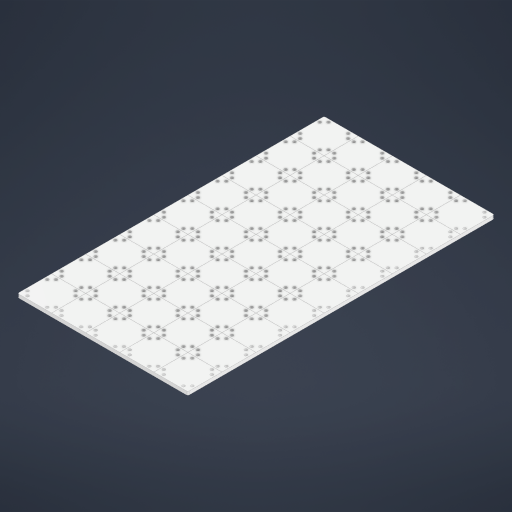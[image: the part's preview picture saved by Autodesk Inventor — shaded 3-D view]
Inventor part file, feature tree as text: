
AUTODESK INVENTOR PART (.ipt)
format: ipt  version: 2023.4 (Build 274418000, 418)  size: 968,704 bytes
history: native  units: mm
features: sketch x2, pattern_linear x2, extrude x1, fillet x1, projected_geometry x1
ambient origin geometry x8: Origin, YZ Plane, XZ Plane, XY Plane, X Axis, Y Axis, Z Axis, Center Point
bodies: Solid1 (feature_tree)
feature tree (7):
  sketch  "Sketch1"  dims[d2=49.8mm d3=49.8mm d4=4.5mm d5=4.5mm d16=5.0mm d17=0.0mm d51=40.0mm d53=360.0deg d77=45.0deg]
  extrude  "Extrusion1"  Depth=5.0mm TaperAngle=0.0deg
  pattern_linear  "Rectangular Pattern1"  Count1=4 Spacing1=360.0deg
  fillet  "Fillet2"  [1 undecoded]
  pattern_linear  "Rectangular Pattern2"  Count1=4 Spacing1=360.0deg
  projected_geometry  "Projected Loop8"
  sketch  "Sketch6"  dims[d78=4.25mm d79=40.0mm d81=360.0deg d93=10.5mm d94=10.5mm d95=4.1mm d96=4.25mm d97=40.0mm d99=360.0deg d101=34.1mm d102=0.0mm d103=45.0deg d128=50.0mm d129=50.0mm d130=5.0mm d131=0.0mm d132=90.0mm d134=50.0mm d135=50.0mm d137=50.0mm d138=2.5mm d139=50.0mm d140=50.0mm d141=0.0675mm d142=0.0675mm d143=0.0mm d144=90.0mm d146=50.0mm d147=50.0mm d149=50.0mm d35=0.5mm d36=0.872665mm d37=0.5mm d38=0.872665mm d59=0.5mm d60=0.872665mm d61=0.5mm d62=0.872665mm d63=0.5mm d64=0.872665mm d73=0.5mm d74=0.872665mm d75=0.5mm d76=0.872665mm]
note: 1 required parameter value undecoded (feature->parameter linkage not recoverable at this tier; creation-order binding heuristic only, values carry confidence <= 0.55)
